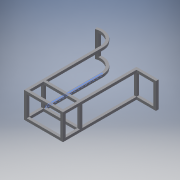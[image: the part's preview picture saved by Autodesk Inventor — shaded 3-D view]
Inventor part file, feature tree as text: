
AUTODESK INVENTOR PART (.ipt)
format: ipt  version: 2017 (Build 210142000, 142)  size: 227,328 bytes
history: native  units: mm
features: extrude x4, sketch x4, projected_geometry x1
ambient origin geometry x8: Origin, YZ Plane, XZ Plane, XY Plane, X Axis, Y Axis, Z Axis, Center Point
bodies: Solid1 (feature_tree)
feature tree (9):
  extrude  "Extrusion1"  Depth=40.0mm
  extrude  "Extrusion2"  Depth=40.0mm
  extrude  "Extrusion3"  Depth=600.0mm
  extrude  "Extrusion4"  Depth=1136.746147mm
  sketch  "Sketch1"  dims[d0=40.0mm d1=40.0mm]
  sketch  "Sketch2"  dims[d2=40.0mm d3=40.0mm]
  sketch  "Sketch3"  dims[d4=40.0mm d6=600.0mm]
  sketch  "Sketch4"  dims[d7=1400.0mm d8=1136.746147mm d9=300.0mm d10=300.0mm d11=19.198622mm d12=400.0mm d13=0.0mm d14=40.0mm d15=40.0mm d16=40.0mm d17=40.0mm d18=40.0mm d19=40.0mm d20=400.0mm d21=0.0mm d22=40.0mm d23=40.0mm d24=160.284942mm d25=400.0mm d26=0.0mm d27=10.0mm d28=0.0mm]
  projected_geometry  "Projected Loop1"
